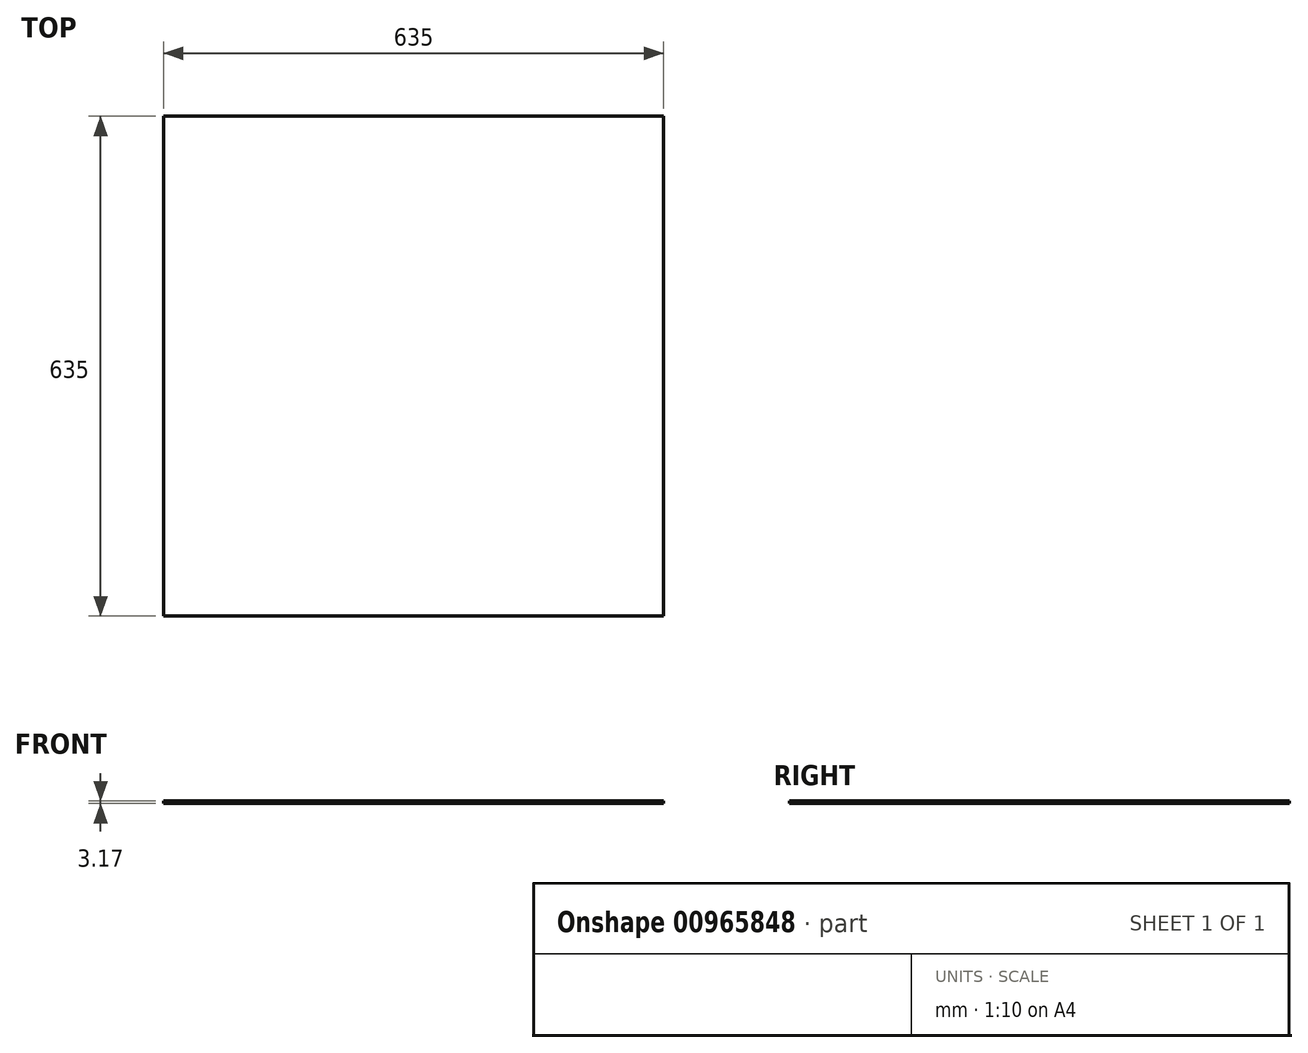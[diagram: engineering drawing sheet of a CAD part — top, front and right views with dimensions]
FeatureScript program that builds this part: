
annotation { "Feature Type Name" : "Feature", "Feature Type Description" : "" }
export const myFeature = defineFeature(function(context is Context, id is Id, definition is map)
    precondition{}
    {
        {
            var Q0;
            Q0=qCreatedBy(makeId("Top.planeOp"),FACE);
            var sketch = newSketch(context, id + "F0", { "sketchPlane" : qUnion([Q0])});
            skLineSegment(sketch, "E0.bottom", {"start": v(-281.52, 416.59) * mm, "end": v(353.48, 416.59) * mm});
            skLineSegment(sketch, "E0.top", {"start": v(-281.52, -218.41) * mm, "end": v(353.48, -218.41) * mm});
            skLineSegment(sketch, "E0.left", {"start": v(-281.52, 416.59) * mm, "end": v(-281.52, -218.41) * mm});
            skLineSegment(sketch, "E0.right", {"start": v(353.48, 416.59) * mm, "end": v(353.48, -218.41) * mm});
            skSolve(sketch);
        }
        {
            var Q0;
            Q0=makeQuery(id+"F0.imprint","IMPRINT",FACE,{"disambiguationData":[TD([[makeQuery(id+"F0.imprint","IMPRINT",EDGE,{"derivedFrom":sQuery(id+"F0.wireOp",EDGE,"E0.bottom")}),-1.0]])]});
            extrude(context, id + "F1", {"entities" : qUnion([Q0]), "depth" : 3.17 * mm, "offsetDistance" : 25.4 * mm});
        }
    });
